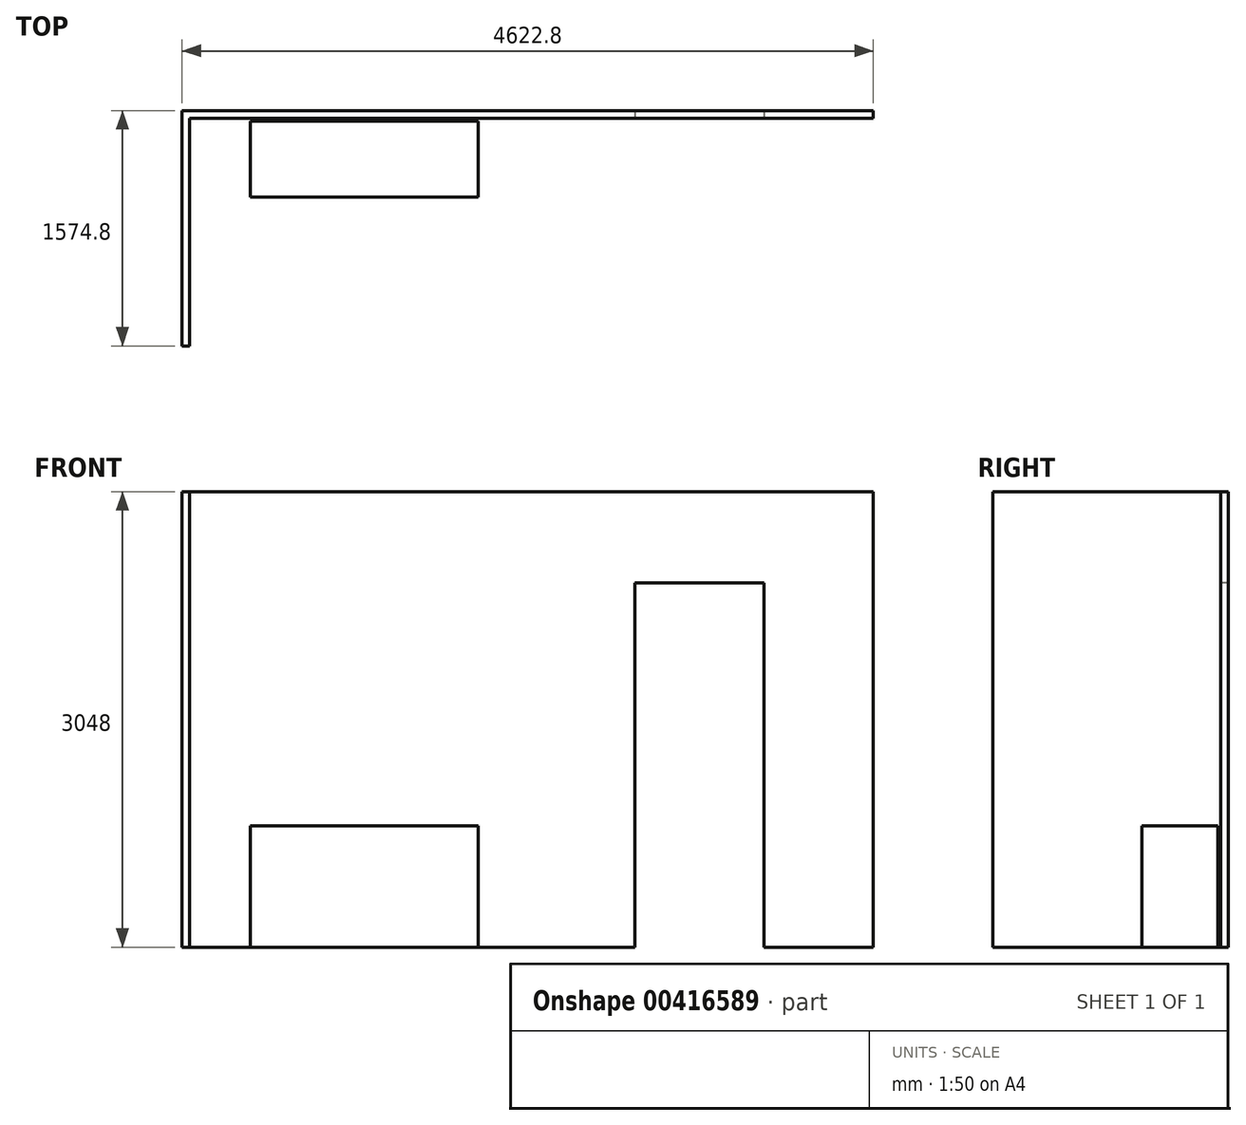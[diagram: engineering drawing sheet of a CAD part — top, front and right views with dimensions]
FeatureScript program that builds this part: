
annotation { "Feature Type Name" : "Feature", "Feature Type Description" : "" }
export const myFeature = defineFeature(function(context is Context, id is Id, definition is map)
    precondition{}
    {
        {
            var Q0;
            Q0=qCreatedBy(makeId("Top.planeOp"),FACE);
            var sketch = newSketch(context, id + "F0", { "sketchPlane" : qUnion([Q0])});
            skLineSegment(sketch, "E0", {"start": v(0, 0) * mm, "end": v(0, 1524) * mm});
            skLineSegment(sketch, "E1", {"start": v(0, 1524) * mm, "end": v(4572, 1524) * mm});
            skLineSegment(sketch, "E2", {"start": v(4572, 1524) * mm, "end": v(4572, 1574.8) * mm});
            skLineSegment(sketch, "E3", {"start": v(4572, 1574.8) * mm, "end": v(-50.8, 1574.8) * mm});
            skLineSegment(sketch, "E4", {"start": v(-50.8, 1574.8) * mm, "end": v(-50.8, 0) * mm});
            skLineSegment(sketch, "E5", {"start": v(-50.8, 0) * mm, "end": v(0, 0) * mm});
            skSolve(sketch);
        }
        {
            var Q0;
            Q0 = qSketchRegion(id + "F0", true);
            extrude(context, id + "F1", {"entities" : qUnion([Q0]), "depth" : 3048 * mm});
        }
        {
            var Q0;
            Q0=qCreatedBy(makeId("Top.planeOp"),FACE);
            var sketch = newSketch(context, id + "F2", { "sketchPlane" : qUnion([Q0])});
            skLineSegment(sketch, "E6.bottom", {"start": v(406.4, 1504.95) * mm, "end": v(1930.4, 1504.95) * mm});
            skLineSegment(sketch, "E6.top", {"start": v(406.4, 996.95) * mm, "end": v(1930.4, 996.95) * mm});
            skLineSegment(sketch, "E6.left", {"start": v(406.4, 1504.95) * mm, "end": v(406.4, 996.95) * mm});
            skLineSegment(sketch, "E6.right", {"start": v(1930.4, 1504.95) * mm, "end": v(1930.4, 996.95) * mm});
            skSolve(sketch);
        }
        {
            var Q0;
            Q0 = qSketchRegion(id + "F2", true);
            extrude(context, id + "F3", {"entities" : qUnion([Q0]), "depth" : 812.8 * mm});
        }
        {
            var Q0;
            Q0=makeQuery(id+"F1.opExtrude","SWEPT_FACE",FACE,{"disambiguationData":[OSD([sQuery(id+"F0.wireOp",EDGE,"E1")])]});
            var sketch = newSketch(context, id + "F4", { "sketchPlane" : qUnion([Q0])});
            skLineSegment(sketch, "E7.bottom", {"start": v(2976.1, 0) * mm, "end": v(3839.7, 0) * mm});
            skLineSegment(sketch, "E7.top", {"start": v(2976.1, 2438.4) * mm, "end": v(3839.7, 2438.4) * mm});
            skLineSegment(sketch, "E7.left", {"start": v(2976.1, 0) * mm, "end": v(2976.1, 2438.4) * mm});
            skLineSegment(sketch, "E7.right", {"start": v(3839.7, 0) * mm, "end": v(3839.7, 2438.4) * mm});
            skSolve(sketch);
        }
        {
            var Q0;
            Q0 = qSketchRegion(id + "F4", true);
            extrude(context, id + "F5", {"entities" : qUnion([Q0]), "operationType" : NewBodyOperationType.REMOVE, "oppositeDirection" : true, "depth" : 50.8 * mm});
        }
    });
